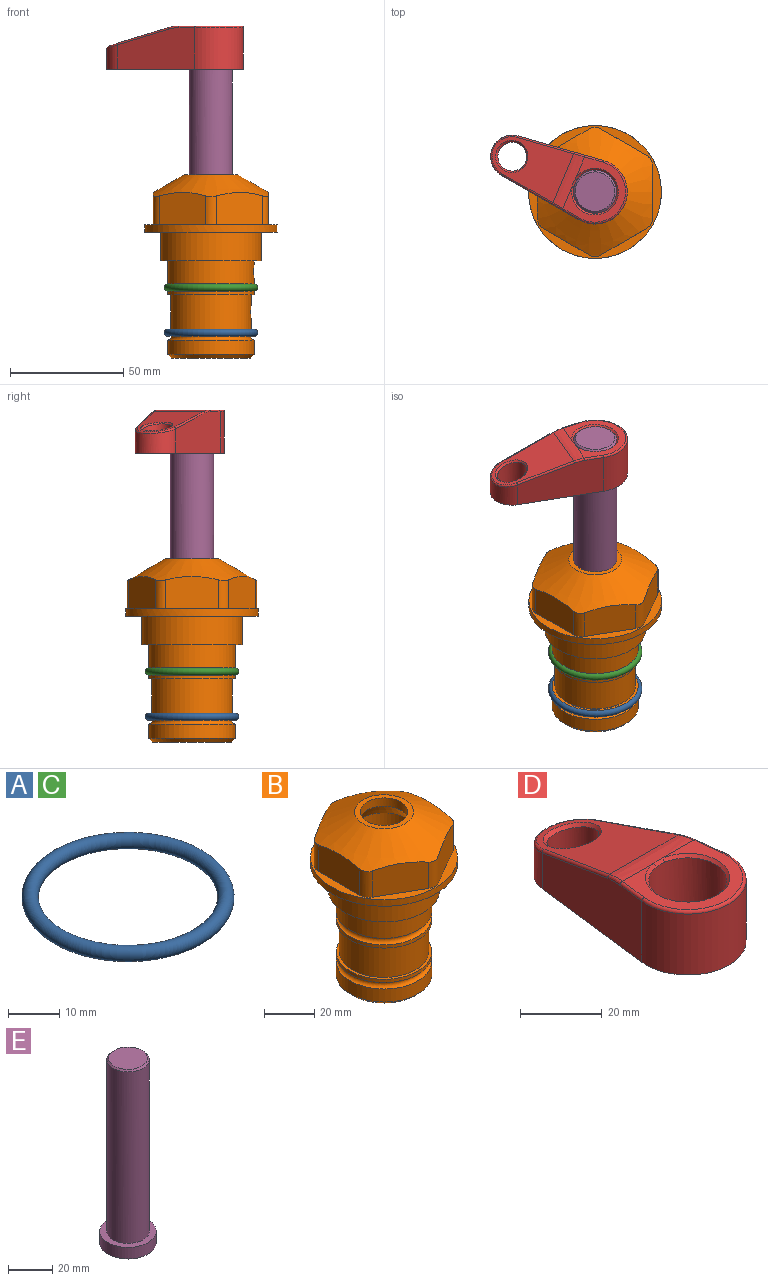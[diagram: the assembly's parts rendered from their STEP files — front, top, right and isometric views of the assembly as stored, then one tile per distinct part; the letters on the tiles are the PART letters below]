
ASSEMBLY  parts=5 mates=4
PART A: 1 faces, bbox 44.7x44.7x3.2 mm
  f0: torus R=19.05mm, axis (0,0,1), area 1193.9mm2
PART B: 36 faces, bbox 58.7x58.7x81 mm
  f0: cylinder r=17.78mm len=35.56mm, axis (0,0,1), area 1670.8mm2, adj f23,f24,f31
  f1: cylinder r=19.05mm len=38.1mm, axis (0,0,1), area 1191.9mm2, adj f26,f27,f30
  f2: plane 58.66x58.66mm, normal (0,0,-1), area 1150.6mm2, adj f3,f28
  f3: cylinder r=29.33mm len=58.66mm, axis (0,0,-1), area 585.1mm2, adj f2,f4
  f4: plane 58.66x58.66mm, normal (0,0,1), area 475.9mm2, adj f3,f5,f6,f7,f8,f9,f10,f11
  f5: plane 20.32x14.34mm, normal (-0.5,0.87,0), area 324.4mm2, adj f4,f15,f16,f17
  f6: plane 20.32x14.34mm, normal (0.5,0.87,0), area 324.4mm2, adj f4,f14,f15,f17
  f7: plane 23.48x14.34mm, normal (1,0,0), area 324.4mm2, adj f4,f13,f14,f17
  f8: plane 20.32x14.34mm, normal (0.5,-0.87,0), area 324.4mm2, adj f4,f12,f13,f17
  f9: plane 20.32x14.34mm, normal (-0.5,-0.87,0), area 324.4mm2, adj f4,f11,f12,f17
  f10: plane 23.48x14.34mm, normal (-1,0,0), area 324.4mm2, adj f4,f11,f16,f17
  f11: cylinder r=5.08mm len=12.85mm, axis (0,0,-1), area 67.2mm2, adj f4,f9,f10,f17
  f12: cylinder r=5.08mm len=12.85mm, axis (0,0,-1), area 67.2mm2, adj f4,f8,f9,f17
  f13: cylinder r=5.08mm len=12.85mm, axis (0,0,-1), area 67.2mm2, adj f4,f7,f8,f17
  f14: cylinder r=5.08mm len=12.85mm, axis (0,0,-1), area 67.2mm2, adj f4,f6,f7,f17
  f15: cylinder r=5.08mm len=12.85mm, axis (0,0,-1), area 67.2mm2, adj f4,f5,f6,f17
  f16: cylinder r=5.08mm len=12.85mm, axis (0,0,-1), area 67.2mm2, adj f4,f5,f10,f17
  f17: cone r=11.73mm half-angle=60deg, axis (0,0,-1), area 2071.8mm2, adj f5,f6,f7,f8,f9,f10,f11,f12
  f18: plane 23.46x23.46mm, normal (0,0,1), area 147.4mm2, adj f17,f35
  f19: plane 34.93x34.93mm, normal (0,0,-1), area 958mm2, adj f29
  f20: cylinder r=19.05mm len=38.1mm, axis (0,0,1), area 760.1mm2, adj f21,f29
  f21: torus R=19.05mm, axis (0,0,1), area 565.3mm2, adj f20,f22
  f22: cylinder r=19.05mm len=38.1mm, axis (0,0,1), area 190mm2, adj f21,f23
  f23: plane 38.1x38.1mm, normal (0,0,1), area 146.9mm2, adj f0,f22
  f24: plane 38.1x38.1mm, normal (0,0,-1), area 146.9mm2, adj f0,f25
  f25: cylinder r=19.05mm len=38.1mm, axis (0,0,1), area 190mm2, adj f24,f26
  f26: torus R=19.05mm, axis (0,0,1), area 565.3mm2, adj f1,f25
  f27: plane 44.45x44.45mm, normal (0,0,-1), area 411.7mm2, adj f1,f28
  f28: cylinder r=22.23mm len=44.45mm, axis (0,0,1), area 1773.5mm2, adj f2,f27
  f29: cone r=19.05mm half-angle=45deg, axis (0,0,1), area 257.5mm2, adj f19,f20
  f30: cylinder r=3.17mm len=6.75mm, axis (-1,0,0), area 128mm2, adj f1,f33
  f31: cylinder r=3.17mm len=6.35mm, axis (-1,0,0), area 102.5mm2, adj f0,f33
  f32: plane 25.4x25.4mm, normal (0,0,1), area 506.7mm2, adj f33
  f33: cylinder r=12.7mm len=66.42mm, axis (0,0,-1), area 5236.2mm2, adj f30,f31,f32,f34
  f34: cone r=9.53mm half-angle=30deg, axis (0,0,-1), area 443.4mm2, adj f33,f35
  f35: cylinder r=9.53mm len=19.05mm, axis (0,0,-1), area 240.9mm2, adj f18,f34
PART C: same geometry as A
PART D: 31 faces, bbox 31.7x65.5x19.8 mm
  f0: plane 39.12x18.26mm, normal (0.99,0.12,0), area 612.2mm2, adj f1,f4,f7,f11,f13,f15
  f1: cylinder r=9.53mm len=18.91mm, axis (0,0,-1), area 296.1mm2, adj f0,f2,f7,f17
  f2: plane 39.12x18.26mm, normal (-0.99,0.12,0), area 612.2mm2, adj f1,f4,f7,f12,f14,f16
  f3: cylinder r=6.35mm len=12.7mm, axis (0,0,-1), area 362.4mm2, adj f7,f18
  f4: cylinder r=14.29mm len=28.58mm, axis (0,0,-1), area 882.2mm2, adj f0,f2,f7,f10
  f5: cylinder r=9.53mm len=19.05mm, axis (0,0,-1), area 1092.6mm2, adj f7,f19,f20
  f6: plane 26.99x23.69mm, normal (0,0,1), area 216.2mm2, adj f9,f10,f11,f12,f19
  f7: plane 63.5x28.58mm, normal (0,0,-1), area 661.8mm2, adj f0,f1,f2,f3,f4,f5,f22,f23
  f8: plane 33.52x23.6mm, normal (0,0.26,0.97), area 486mm2, adj f9,f15,f16,f17,f18
  f9: cylinder r=19.05mm len=24.72mm, axis (1,0,0), area 120.4mm2, adj f6,f8,f13,f14,f20
  f10: torus R=13.49mm, axis (0,0,1), area 59mm2, adj f4,f6,f11,f12
  f11: cylinder r=0.79mm len=8.67mm, axis (0.12,-0.99,0), area 10.8mm2, adj f0,f6,f10,f13
  f12: cylinder r=0.79mm len=8.67mm, axis (0.12,0.99,0), area 10.8mm2, adj f2,f6,f10,f14
  f13: bspline ~4.95x1.42mm, area 6.1mm2, adj f0,f9,f11,f15
  f14: bspline ~4.95x1.42mm, area 6.1mm2, adj f2,f9,f12,f16
  f15: cylinder r=0.79mm len=25.95mm, axis (0.12,-0.96,0.26), area 32.9mm2, adj f0,f8,f13,f17
  f16: cylinder r=0.79mm len=25.95mm, axis (0.12,0.96,-0.26), area 32.9mm2, adj f2,f8,f14,f17
  f17: bspline ~18.91x8.38mm, area 30mm2, adj f1,f8,f15,f16
  f18: bspline ~14.29x14.29mm, area 48.3mm2, adj f3,f8
  f19: cone r=9.53mm half-angle=45deg, axis (0,0,1), area 66.5mm2, adj f5,f6,f20
  f20: bspline ~3.22x0.96mm, area 3.5mm2, adj f5,f9,f19
  f21: plane 2.75x2.72mm, normal (0,0,-1), area 2.9mm2, adj f23,f25,f28
  f22: plane 23.05x15.88mm, normal (-0.99,-0.12,0), area 323.6mm2, adj f7,f25,f26,f27,f28,f29
  f23: plane 23.05x15.88mm, normal (0.99,-0.12,0), area 323.6mm2, adj f7,f21,f25,f27,f28,f30
  f24: cylinder r=9.53mm len=10.69mm, axis (0,0,-1), area 114.7mm2, adj f7,f27,f29,f30
  f25: cylinder r=12.7mm len=20.59mm, axis (0,0,-1), area 381.1mm2, adj f7,f21,f22,f23,f26,f28
  f26: plane 2.75x2.72mm, normal (0,0,-1), area 2.9mm2, adj f22,f25,f28
  f27: plane 19.72x18.37mm, normal (0,-0.26,-0.97), area 291.8mm2, adj f22,f23,f24,f28,f29,f30
  f28: cylinder r=15.88mm len=19.92mm, axis (1,0,0), area 54.8mm2, adj f21,f22,f23,f25,f26,f27
  f29: cylinder r=1.59mm len=11mm, axis (0,0,-1), area 34.7mm2, adj f7,f22,f24,f27
  f30: cylinder r=1.59mm len=11mm, axis (0,0,-1), area 34.7mm2, adj f7,f23,f24,f27
PART E: 6 faces, bbox 25.4x25.4x101.6 mm
  f0: plane 17.46x17.46mm, normal (0,0,1), area 239.5mm2, adj f5
  f1: plane 25.4x25.4mm, normal (0,0,-1), area 506.7mm2, adj f2
  f2: cylinder r=12.7mm len=25.4mm, axis (0,0,1), area 506.7mm2, adj f1,f3
  f3: plane 25.4x25.4mm, normal (0,0,1), area 221.7mm2, adj f2,f4
  f4: cylinder r=9.53mm len=94.46mm, axis (0,0,1), area 5653mm2, adj f3,f5
  f5: cone r=8.73mm half-angle=45deg, axis (0,0,-1), area 64.4mm2, adj f0,f4
PLACE A t=(0,0,-20)mm
PLACE B at identity fixed
PLACE C at identity
PLACE D rot(axis=(0,0,1),67.1deg) t=(0,0,27.55)mm
PLACE E rot(axis=(0,0,1),67.1deg) t=(0,0,27.55)mm
MATE cylindrical E.f2 <-> B.f0  axis (0,0,-1) through (0,0,-10.55)mm
MATE fastened A.f0 <-> B.f0  axis (0,0,1) through (0,0,-44.51)mm
MATE fastened E.f2 <-> D.f4  axis (0,0,1) through (0,0,91.05)mm
MATE fastened C.f0 <-> B.f0  axis (0,0,1) through (0,0,-24.51)mm
